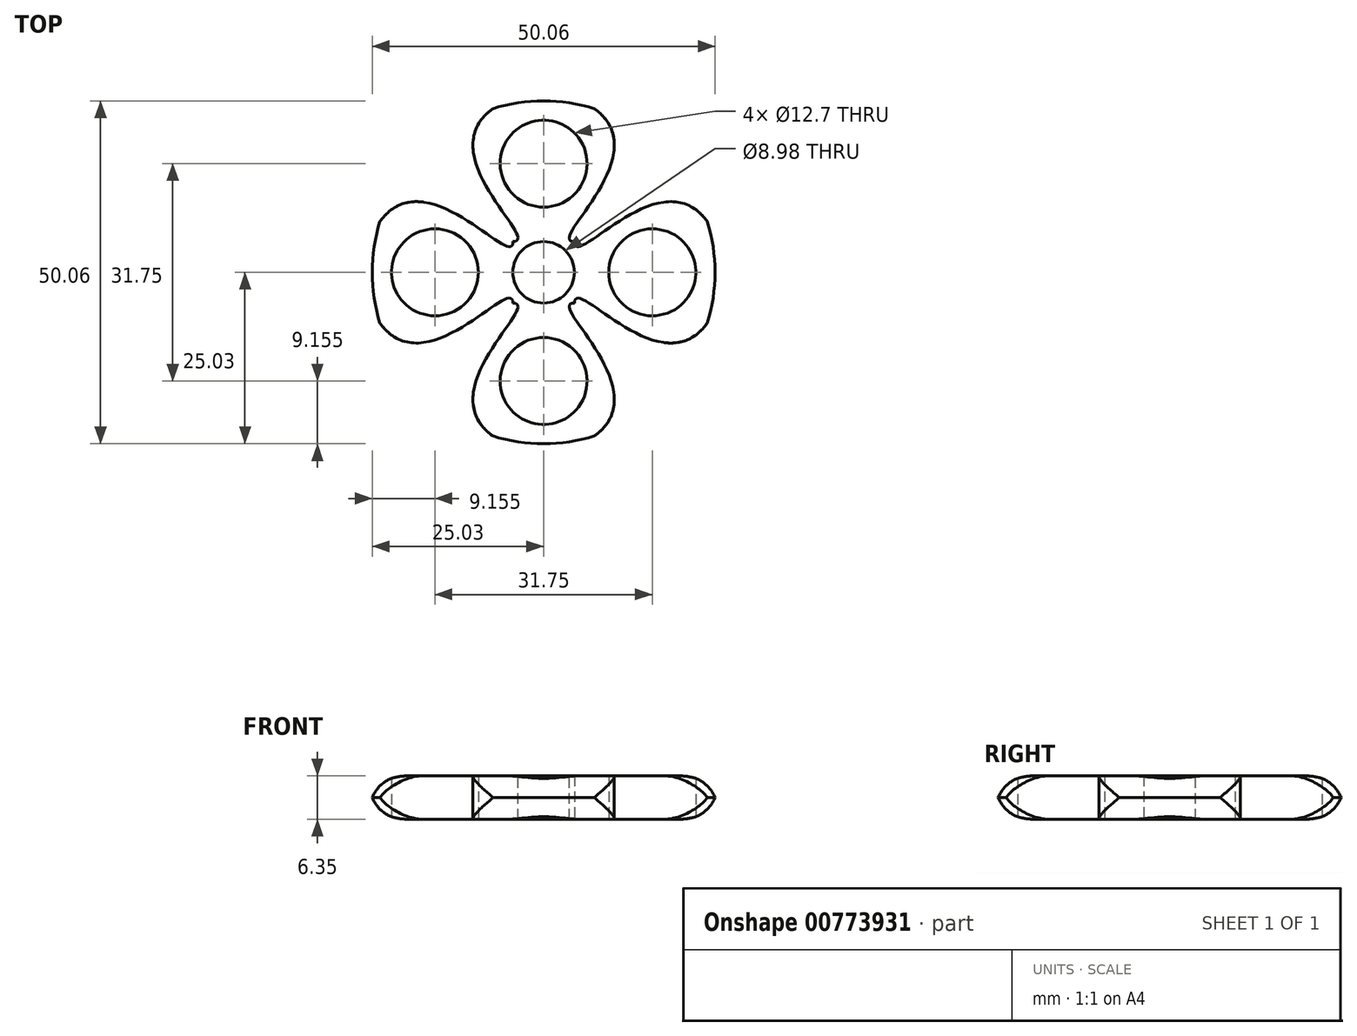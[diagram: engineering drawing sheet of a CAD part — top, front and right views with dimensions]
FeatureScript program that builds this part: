
annotation { "Feature Type Name" : "Feature", "Feature Type Description" : "" }
export const myFeature = defineFeature(function(context is Context, id is Id, definition is map)
    precondition{}
    {
        {
            var Q0;
            Q0=qCreatedBy(makeId("Top.planeOp"),FACE);
            var sketch = newSketch(context, id + "F0", { "sketchPlane" : qUnion([Q0])});
            skArc(sketch, "E0", {"start": v(6.35, 24.6) * mm, "mid": v(0, 25.4) * mm, "end": v(-6.35, 24.6) * mm});
            skCircle(sketch, "E1", {"center": v(0, 15.88) * mm, "radius": 6.35 * mm});
            skLineSegment(sketch, "E2", {"start": v(0, 0) * mm, "end": v(-4.5, 4.5) * mm, "construction": true});
            skLineSegment(sketch, "E3", {"start": v(-6.35, 15.88) * mm, "end": v(-6.35, 24.6) * mm, "construction": true});
            skFitSpline(sketch, "E4", {"points": [v(-4.5, 4.5) * mm, v(-6.35, 24.6) * mm], "startDerivative": vector(13.47, 0) * mm, "endDerivative": vector(34.83, 19.9) * mm});
            skFitSpline(sketch, "E5.MirrorCS", {"points": [v(4.5, 4.5) * mm, v(6.35, 24.6) * mm], "startDerivative": vector(-13.47, 0) * mm, "endDerivative": vector(-34.83, 19.9) * mm});
            skCircle(sketch, "E6.1.0", {"center": v(-15.88, 0) * mm, "radius": 6.35 * mm});
            skArc(sketch, "E6.1.1", {"start": v(-24.6, 6.35) * mm, "mid": v(-25.4, 0) * mm, "end": v(-24.6, -6.35) * mm});
            skCircle(sketch, "E6.2.0", {"center": v(0, -15.88) * mm, "radius": 6.35 * mm});
            skArc(sketch, "E6.2.1", {"start": v(-6.35, -24.6) * mm, "mid": v(0, -25.4) * mm, "end": v(6.35, -24.6) * mm});
            skCircle(sketch, "E6.3.0", {"center": v(15.88, 0) * mm, "radius": 6.35 * mm});
            skArc(sketch, "E6.3.1", {"start": v(24.6, -6.35) * mm, "mid": v(25.4, 0) * mm, "end": v(24.6, 6.35) * mm});
            skFitSpline(sketch, "E7", {"points": [v(4.5, 4.5) * mm, v(24.6, 6.35) * mm], "startDerivative": vector(0, -13.47) * mm, "endDerivative": vector(19.9, -34.83) * mm});
            skLineSegment(sketch, "E8", {"start": v(-4.5, 4.5) * mm, "end": v(4.5, -4.5) * mm, "construction": true});
            skLineSegment(sketch, "E9", {"start": v(4.5, 4.5) * mm, "end": v(0, 0) * mm, "construction": true});
            skLineSegment(sketch, "E10", {"start": v(4.5, 4.5) * mm, "end": v(-4.5, -4.5) * mm, "construction": true});
            skLineSegment(sketch, "E11", {"start": v(0, 0) * mm, "end": v(22.5, 22.5) * mm, "construction": true});
            skLineSegment(sketch, "E12", {"start": v(-4.5, 4.5) * mm, "end": v(4.5, 4.5) * mm, "construction": true});
            skLineSegment(sketch, "E13", {"start": v(4.5, -4.5) * mm, "end": v(4.5, 4.5) * mm, "construction": true});
            skLineSegment(sketch, "E14", {"start": v(4.5, -4.5) * mm, "end": v(-4.5, -4.5) * mm, "construction": true});
            skLineSegment(sketch, "E15", {"start": v(-4.5, -4.5) * mm, "end": v(-4.5, 4.5) * mm, "construction": true});
            skFitSpline(sketch, "E16.MirrorCS", {"points": [v(4.5, -4.5) * mm, v(24.6, -6.35) * mm], "startDerivative": vector(0, 13.47) * mm, "endDerivative": vector(19.9, 34.83) * mm});
            skLineSegment(sketch, "E17", {"start": v(-4.5, 4.5) * mm, "end": v(21.02, -21.02) * mm, "construction": true});
            skLineSegment(sketch, "E18", {"start": v(4.5, 4.5) * mm, "end": v(-25.18, -25.18) * mm, "construction": true});
            skFitSpline(sketch, "E19", {"points": [v(4.5, -4.5) * mm, v(6.35, -24.6) * mm], "startDerivative": vector(-13.47, 0) * mm, "endDerivative": vector(-34.83, -19.9) * mm});
            skFitSpline(sketch, "E20", {"points": [v(-4.5, -4.5) * mm, v(-24.6, -6.35) * mm], "startDerivative": vector(0, 13.47) * mm, "endDerivative": vector(-19.9, 34.83) * mm});
            skFitSpline(sketch, "E21.MirrorCS", {"points": [v(-4.5, -4.5) * mm, v(-6.35, -24.6) * mm], "startDerivative": vector(13.47, 0) * mm, "endDerivative": vector(34.83, -19.9) * mm});
            skFitSpline(sketch, "E22.MirrorCS", {"points": [v(-4.5, 4.5) * mm, v(-24.6, 6.35) * mm], "startDerivative": vector(0, -13.47) * mm, "endDerivative": vector(-19.9, -34.83) * mm});
            skCircle(sketch, "E23", {"center": v(0, 0) * mm, "radius": 4.5 * mm});
            skSolve(sketch);
        }
        {
            var Q0;
            Q0 = qSketchRegion(id + "F0", true);
            extrude(context, id + "F1", {"entities" : qUnion([Q0]), "depth" : 6.35 * mm, "offsetDistance" : 25.4 * mm});
        }
        {
            var Q0;
            Q0=makeQuery(id+"F1.opExtrude","CAP_EDGE",EDGE,{"disambiguationData":[OSD([sQuery(id+"F0.wireOp",EDGE,"E0")])],"isStart":false});
            var Q1;
            Q1=makeQuery(id+"F1.opExtrude","CAP_EDGE",EDGE,{"disambiguationData":[OSD([sQuery(id+"F0.wireOp",EDGE,"E0")])],"isStart":true});
            var Q2;
            Q2=makeQuery(id+"F1.opExtrude","CAP_EDGE",EDGE,{"disambiguationData":[OSD([sQuery(id+"F0.wireOp",EDGE,"E6.3.1")])],"isStart":false});
            var Q3;
            Q3=makeQuery(id+"F1.opExtrude","CAP_EDGE",EDGE,{"disambiguationData":[OSD([sQuery(id+"F0.wireOp",EDGE,"E6.3.1")])],"isStart":true});
            var Q4;
            Q4=makeQuery(id+"F1.opExtrude","CAP_EDGE",EDGE,{"disambiguationData":[OSD([sQuery(id+"F0.wireOp",EDGE,"E6.2.1")])],"isStart":false});
            var Q5;
            Q5=makeQuery(id+"F1.opExtrude","CAP_EDGE",EDGE,{"disambiguationData":[OSD([sQuery(id+"F0.wireOp",EDGE,"E6.2.1")])],"isStart":true});
            var Q6;
            Q6=makeQuery(id+"F1.opExtrude","CAP_EDGE",EDGE,{"disambiguationData":[OSD([sQuery(id+"F0.wireOp",EDGE,"E6.1.1")])],"isStart":false});
            var Q7;
            Q7=makeQuery(id+"F1.opExtrude","CAP_EDGE",EDGE,{"disambiguationData":[OSD([sQuery(id+"F0.wireOp",EDGE,"E6.1.1")])],"isStart":true});
            fillet(context, id + "F2", {"entities" : qUnion([Q0, Q1, Q2, Q3, Q4, Q5, Q6, Q7]), "radius" : 5.08 * mm, "tangentPropagation" : true, "allowEdgeOverflow" : false});
        }
    });
